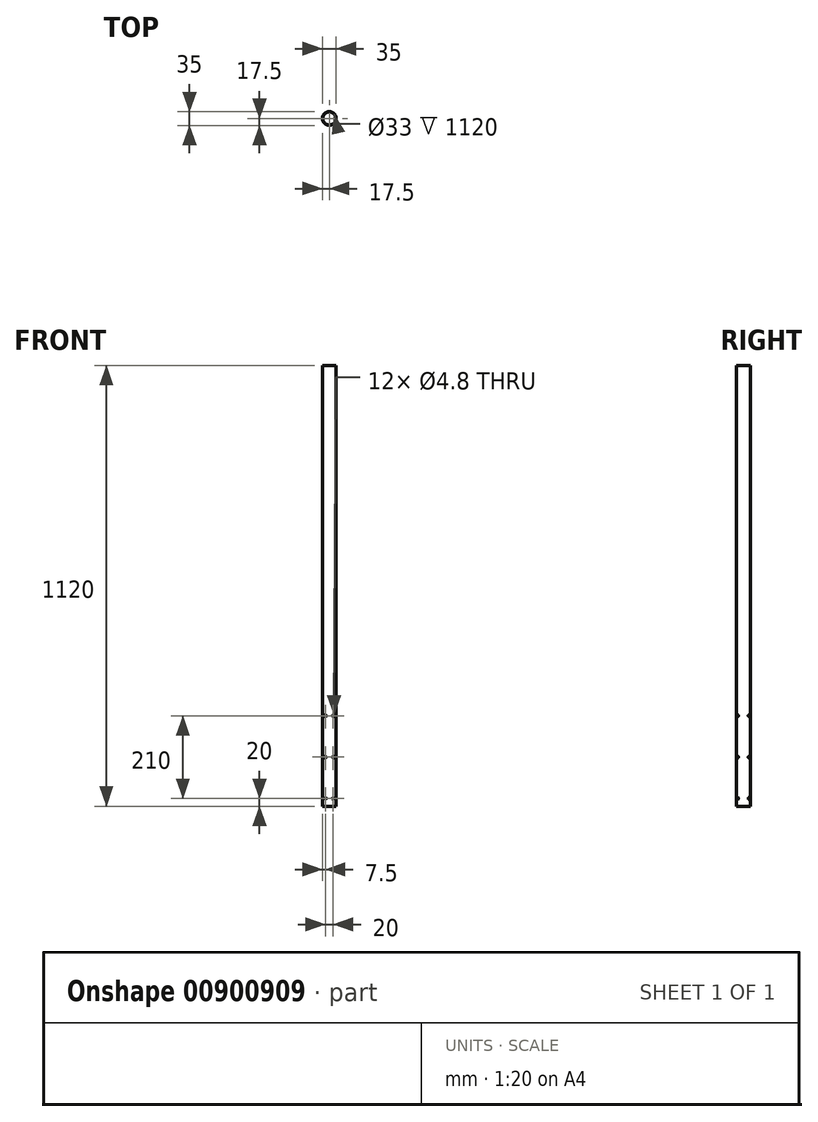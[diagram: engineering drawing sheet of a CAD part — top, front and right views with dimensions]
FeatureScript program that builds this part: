
annotation { "Feature Type Name" : "Feature", "Feature Type Description" : "" }
export const myFeature = defineFeature(function(context is Context, id is Id, definition is map)
    precondition{}
    {
        {
            var Q0;
            Q0=qCreatedBy(makeId("Top.planeOp"),FACE);
            var sketch = newSketch(context, id + "F0", { "sketchPlane" : qUnion([Q0])});
            skCircle(sketch, "E0", {"center": v(0, 0) * mm, "radius": 17.5 * mm});
            skSolve(sketch);
        }
        {
            var Q0;
            Q0=makeQuery(id+"F0.imprint","IMPRINT",FACE,{"disambiguationData":[TD([[makeQuery(id+"F0.imprint","IMPRINT",EDGE,{"derivedFrom":sQuery(id+"F0.wireOp",EDGE,"E0")}),1.0]])]});
            extrude(context, id + "F1", {"entities" : qUnion([Q0]), "depth" : 1120 * mm, "offsetDistance" : 25 * mm});
        }
        {
            var Q0;
            Q0=sQuery(id+"F0.wireOp",VERTEX,"E0.center");
            var Q1;
            Q1=makeQuery(id+"F1.opExtrude","SWEPT_BODY",BODY,{"disambiguationData":[OSD([sQuery(id+"F0.wireOp",EDGE,"E0")])]});
            hole(context, id + "F2", {"style" : HoleStyle.SIMPLE, "endStyle" : HoleEndStyle.THROUGH, "oppositeDirection" : true, "holeDiameter" : 33 * mm, "majorDiameter" : 5 * mm, "isTappedThrough" : true, "tappedDepth" : 12 * mm, "tapClearance" : 3, "locations" : qUnion([Q0]), "scope" : qUnion([Q1])});
        }
        {
            var Q0;
            Q0=qCreatedBy(makeId("Front.planeOp"),FACE);
            var sketch = newSketch(context, id + "F3", { "sketchPlane" : qUnion([Q0])});
            skLineSegment(sketch, "E1", {"start": v(0, 0) * mm, "end": v(0, 20) * mm});
            skCircle(sketch, "E2", {"center": v(10, 20) * mm, "radius": 2.4 * mm});
            skCircle(sketch, "E3", {"center": v(-10, 20) * mm, "radius": 2.4 * mm});
            skCircle(sketch, "E4", {"center": v(10, 125) * mm, "radius": 2.4 * mm});
            skCircle(sketch, "E5", {"center": v(-10, 125) * mm, "radius": 2.4 * mm});
            skLineSegment(sketch, "E6", {"start": v(-12.4, 125) * mm, "end": v(10, 125) * mm});
            skCircle(sketch, "E7.MirrorC", {"center": v(-10, 230) * mm, "radius": 2.4 * mm});
            skCircle(sketch, "E8.MirrorC", {"center": v(10, 230) * mm, "radius": 2.4 * mm});
            skSolve(sketch);
        }
        {
            var Q0;
            Q0 = qSketchRegion(id + "F3", true);
            extrude(context, id + "F4", {"entities" : qUnion([Q0]), "operationType" : NewBodyOperationType.REMOVE, "oppositeDirection" : true, "depth" : 25 * mm, "offsetDistance" : 25 * mm, "hasSecondDirection" : true, "secondDirectionOppositeDirection" : false, "secondDirectionDepth" : 25 * mm});
        }
    });
